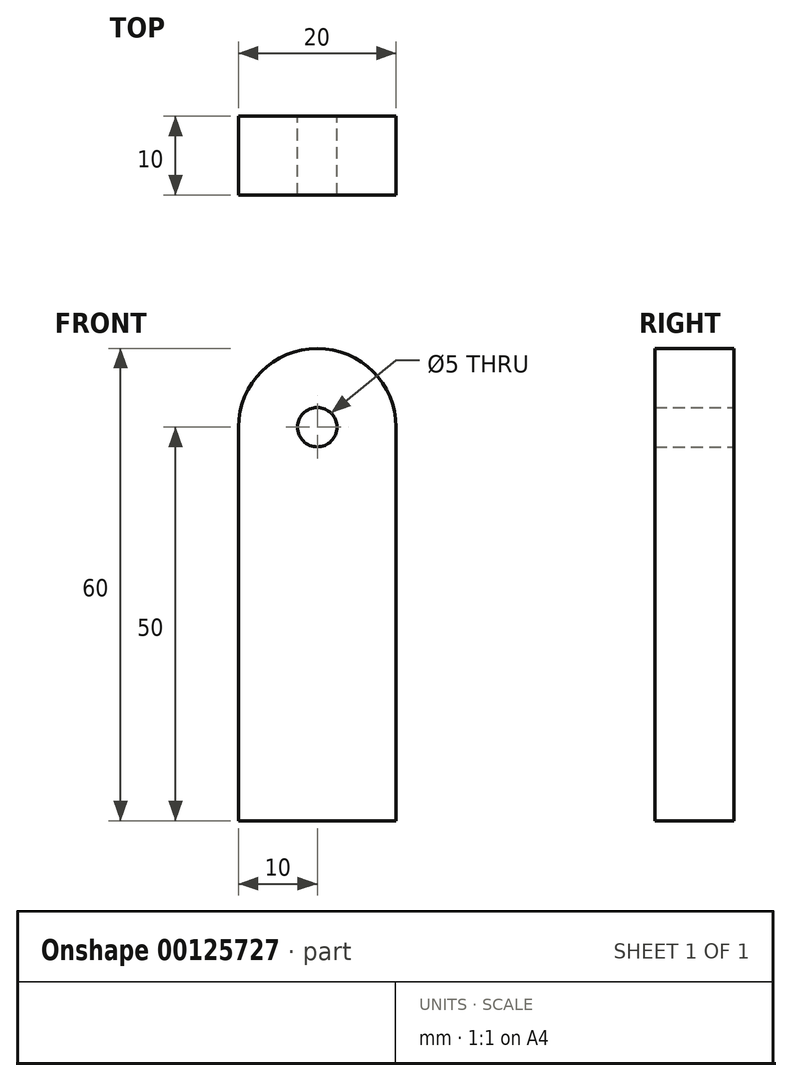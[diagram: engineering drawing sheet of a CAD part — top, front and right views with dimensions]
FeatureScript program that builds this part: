
annotation { "Feature Type Name" : "Feature", "Feature Type Description" : "" }
export const myFeature = defineFeature(function(context is Context, id is Id, definition is map)
    precondition{}
    {
        {
            var Q0;
            Q0=qCreatedBy(makeId("Front.planeOp"),FACE);
            var sketch = newSketch(context, id + "F0", { "sketchPlane" : qUnion([Q0])});
            skLineSegment(sketch, "E0.bottom", {"start": v(-10, 25) * mm, "end": v(10, 25) * mm, "construction": true});
            skLineSegment(sketch, "E0.top", {"start": v(-10, -25) * mm, "end": v(10, -25) * mm});
            skLineSegment(sketch, "E0.left", {"start": v(-10, 25) * mm, "end": v(-10, -25) * mm});
            skLineSegment(sketch, "E0.right", {"start": v(10, 25) * mm, "end": v(10, -25) * mm});
            skPoint(sketch, "E0.middle", {"position": v(0, 0) * mm});
            skArc(sketch, "E1", {"start": v(-10, 25) * mm, "mid": v(0, 35) * mm, "end": v(10, 25) * mm});
            skCircle(sketch, "E2", {"center": v(0, 25) * mm, "radius": 2.5 * mm});
            skSolve(sketch);
        }
        {
            var Q0;
            Q0 = qSketchRegion(id + "F0", true);
            extrude(context, id + "F1", {"entities" : qUnion([Q0]), "depth" : 10 * mm, "symmetric" : true});
        }
    });
